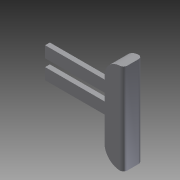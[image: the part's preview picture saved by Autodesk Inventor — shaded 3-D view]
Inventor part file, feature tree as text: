
AUTODESK INVENTOR PART (.ipt)
format: ipt  version: 2012 SP2 (Build 160219200, 219)  size: 116,224 bytes
history: native  units: in
note: dims shown in document units (in); Inventor stores cm internally (conversion verified against a paired STEP export)
features: extrude x3, sketch x3, fillet x2, reference x1
ambient origin geometry x8: Origin, YZ Plane, XZ Plane, XY Plane, X Axis, Y Axis, Z Axis, Center Point
bodies: Solid1 (feature_tree)
feature tree (9):
  extrude  "Extrusion1"  Depth=0.3937in
  fillet  "Fillet1"  Radius=0.3937in
  fillet  "Fillet2"  Radius=0.3287in
  extrude  "Extrusion2"  Depth=0.0394in
  extrude  "Extrusion3"  Depth=0.2362in
  sketch  "Sketch1"  dims[d0=0.2362in d1=0.3937in d2=0.3937in d3=0.0in d4=0.3287in]
  sketch  "Sketch2"  dims[d5=0.0787in d6=0.0394in]
  reference  "Reference1"
  sketch  "Sketch3"  dims[d7=0.0787in d8=0.2362in d9=0.2362in d10=0.7874in d12=0.3937in d13=0.3937in d15=0.3937in d17=1.3937in d18=0.0in d19=0.2165in d20=0.8661in d21=0.1969in d22=0.0in d23=0.2362in]
